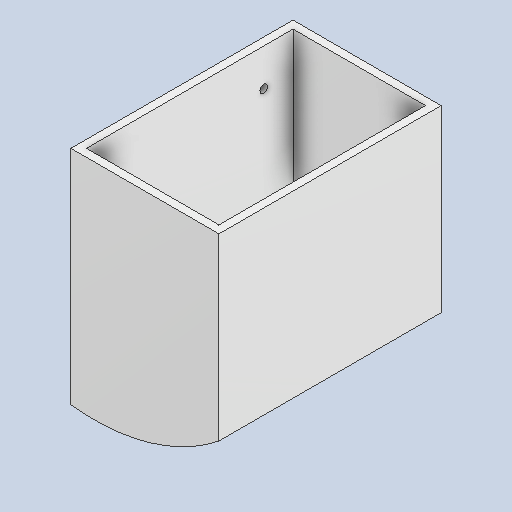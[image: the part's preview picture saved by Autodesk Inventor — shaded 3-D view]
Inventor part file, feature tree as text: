
AUTODESK INVENTOR PART (.ipt)
format: ipt  version: 2022 (Build 260153070, 153G)  size: 130,048 bytes
history: native  units: mm
features: extrude x3, sketch x3
ambient origin geometry x8: Origin, YZ Plane, XZ Plane, XY Plane, X Axis, Y Axis, Z Axis, Center Point
bodies: Solid1 (feature_tree)
feature tree (6):
  extrude  "Extrusion1"  Depth=76.2mm
  extrude  "Extrusion2"  Depth=4.0mm
  extrude  "Extrusion3"  Depth=4.0mm
  sketch  "Sketch1"  dims[d0=114.3mm d1=76.2mm]
  sketch  "Sketch2"  dims[d2=114.3mm d3=0.0mm d4=4.0mm]
  sketch  "Sketch3"  dims[d5=4.0mm d6=4.0mm d7=4.0mm d8=90.0mm d9=0.0mm d10=4.0mm d11=4.0mm d12=4.0mm d13=4.0mm d14=19.05mm d15=19.05mm d16=19.05mm d17=19.05mm d18=19.05mm d19=19.05mm d20=19.05mm d21=19.05mm d22=4.0mm d23=0.0mm]
